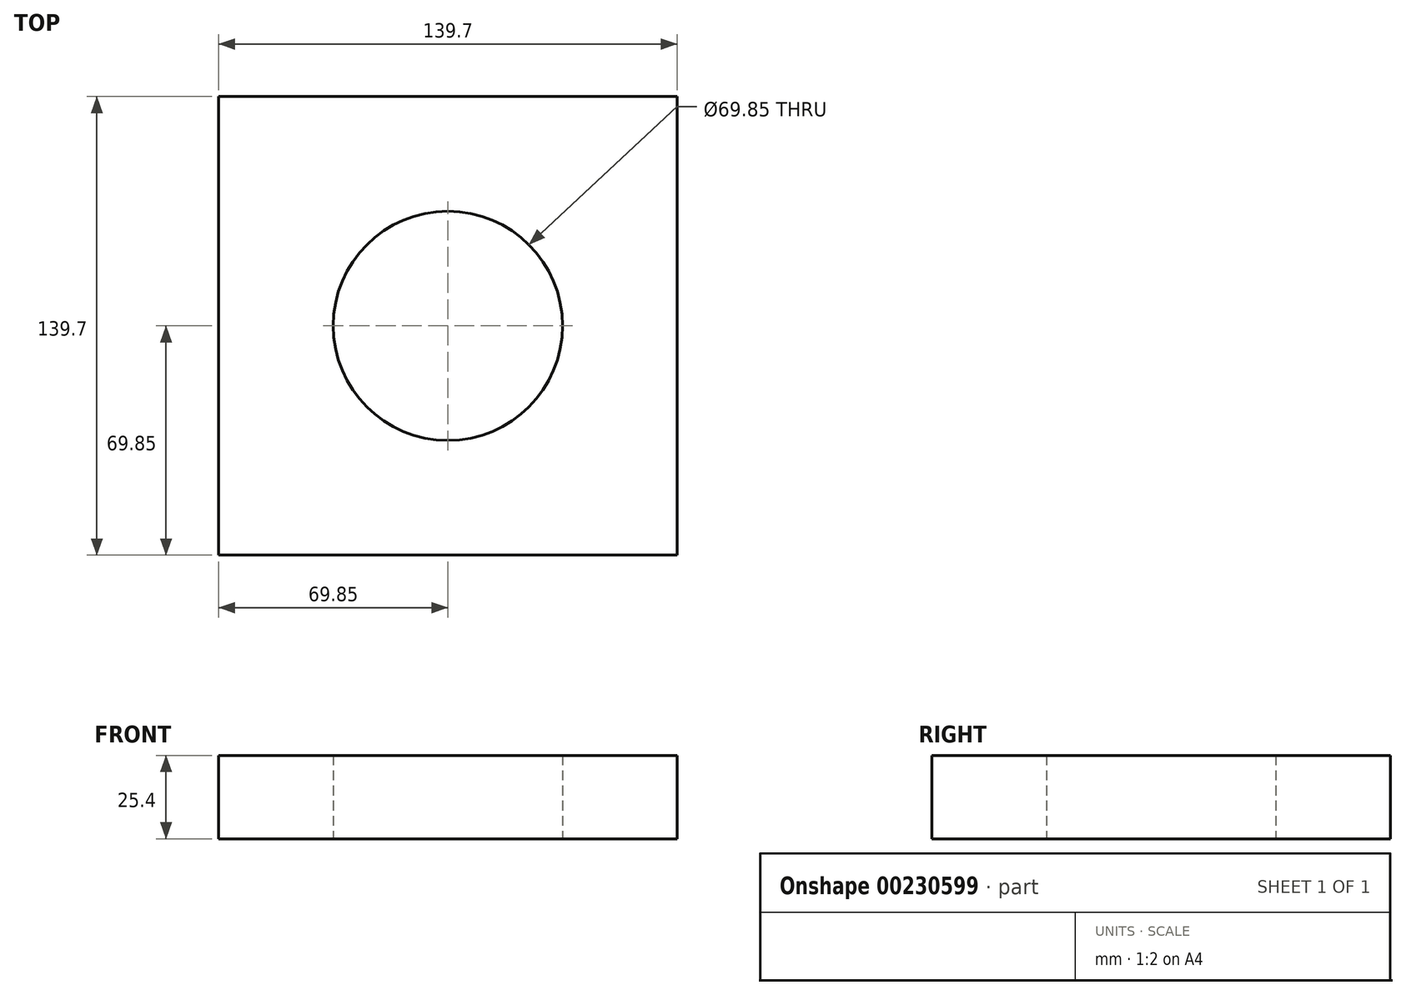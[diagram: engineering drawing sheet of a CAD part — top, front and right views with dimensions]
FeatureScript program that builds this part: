
annotation { "Feature Type Name" : "Feature", "Feature Type Description" : "" }
export const myFeature = defineFeature(function(context is Context, id is Id, definition is map)
    precondition{}
    {
        {
            var Q0;
            Q0=qCreatedBy(makeId("Top.planeOp"),FACE);
            var sketch = newSketch(context, id + "F0", { "sketchPlane" : qUnion([Q0])});
            skLineSegment(sketch, "E0.bottom", {"start": v(-69.85, 69.85) * mm, "end": v(69.85, 69.85) * mm});
            skLineSegment(sketch, "E0.top", {"start": v(-69.85, -69.85) * mm, "end": v(69.85, -69.85) * mm});
            skLineSegment(sketch, "E0.left", {"start": v(-69.85, 69.85) * mm, "end": v(-69.85, -69.85) * mm});
            skLineSegment(sketch, "E0.right", {"start": v(69.85, 69.85) * mm, "end": v(69.85, -69.85) * mm});
            skPoint(sketch, "E0.middle", {"position": v(0, 0) * mm});
            skCircle(sketch, "E1", {"center": v(0, 0) * mm, "radius": 34.93 * mm});
            skSolve(sketch);
        }
        {
            var Q0;
            Q0 = qSketchRegion(id + "F0", true);
            extrude(context, id + "F1", {"entities" : qUnion([Q0]), "depth" : 25.4 * mm});
        }
    });
